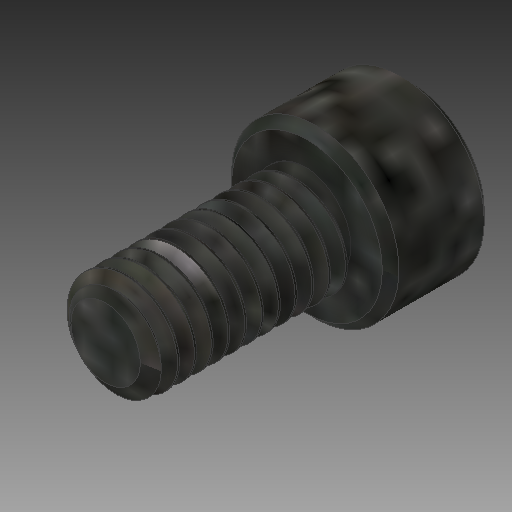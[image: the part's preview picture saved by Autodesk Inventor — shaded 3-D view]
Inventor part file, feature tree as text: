
AUTODESK INVENTOR PART (.ipt)
format: ipt  version: 2018 (Build 220112000, 112)  size: 616,448 bytes
history: native  units: in
note: dims shown in document units (in); Inventor stores cm internally (conversion verified against a paired STEP export)
features: chamfer x1
ambient origin geometry x8: Origin, YZ Plane, XZ Plane, XY Plane, X Axis, Y Axis, Z Axis, Center Point
bodies: Solid1 (feature_tree)
feature tree (1):
  chamfer  "Chamfer1"  [1 undecoded]
note: 1 required parameter value undecoded (feature->parameter linkage not recoverable at this tier; creation-order binding heuristic only, values carry confidence <= 0.55)
